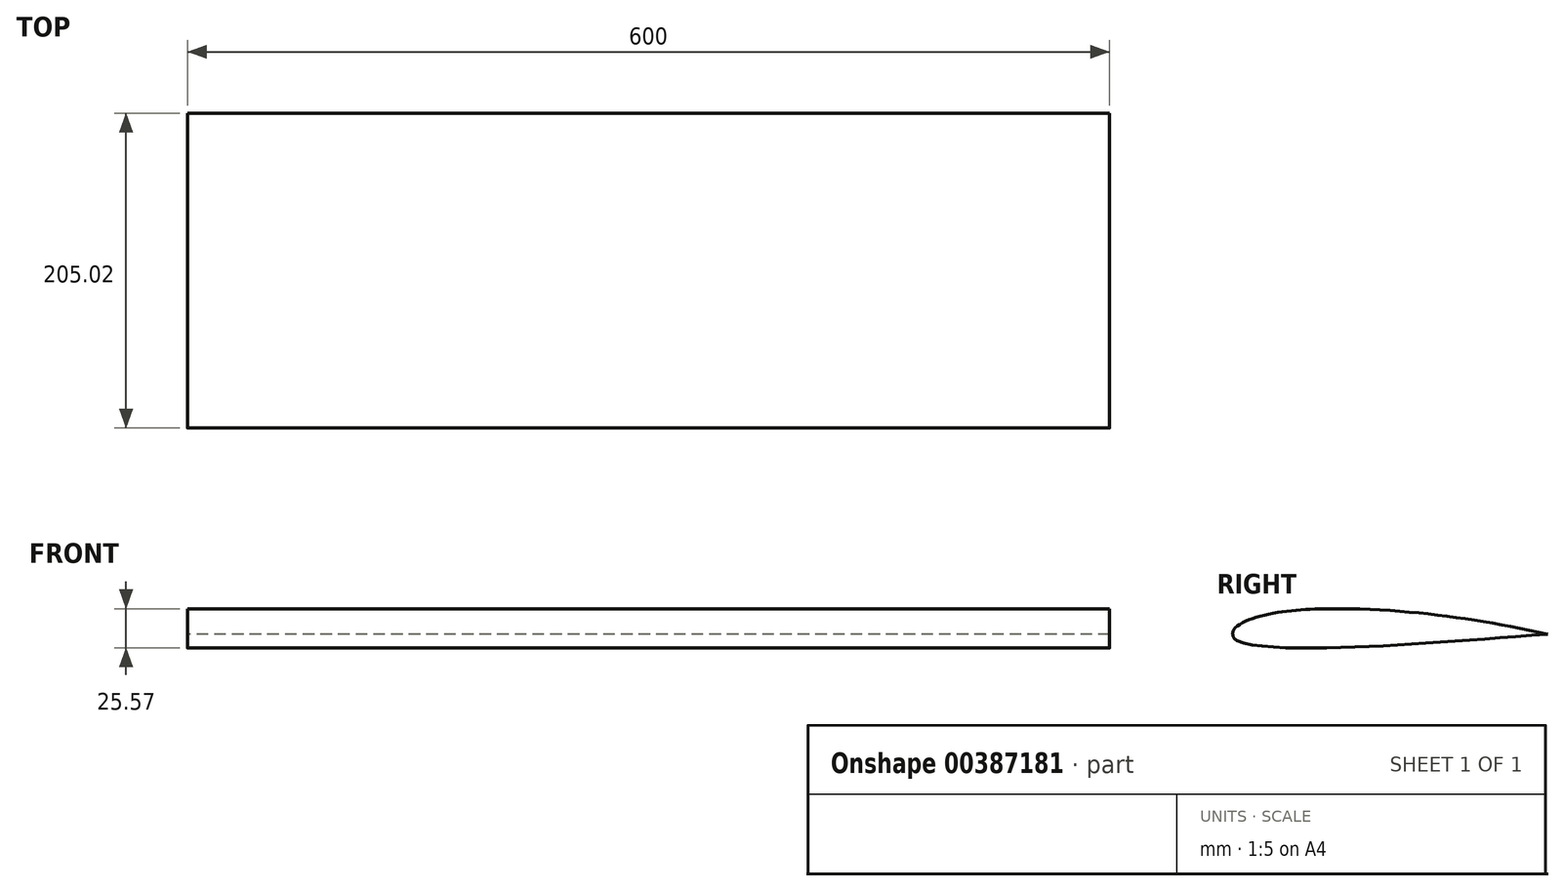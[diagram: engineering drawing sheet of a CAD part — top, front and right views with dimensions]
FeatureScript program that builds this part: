
annotation { "Feature Type Name" : "Feature", "Feature Type Description" : "" }
export const myFeature = defineFeature(function(context is Context, id is Id, definition is map)
    precondition{}
    {
        {
            var Q0;
            Q0=qCreatedBy(makeId("Right.planeOp"),FACE);
            var sketch = newSketch(context, id + "F0", { "sketchPlane" : qUnion([Q0])});
            skSolve(sketch);
        }
        {
            var Q0;
            Q0=qCreatedBy(makeId("Right.planeOp"),FACE);
            var sketch = newSketch(context, id + "F1", { "sketchPlane" : qUnion([Q0])});
            skFitSpline(sketch, "E0", {"points": [v(0, 12.7) * mm, v(-63.5, -3.82) * mm], "startDerivative": vector(-71.79, -0.2) * mm, "endDerivative": vector(-17.43, -38.36) * mm});
            skLineSegment(sketch, "E1", {"start": v(-63.5, -3.82) * mm, "end": v(142.88, -3.82) * mm, "construction": true});
            skFitSpline(sketch, "E2", {"points": [v(0, 12.7) * mm, v(142.88, -3.82) * mm], "startDerivative": vector(161.96, 0.45) * mm, "endDerivative": vector(140.23, -29.51) * mm});
            skFitSpline(sketch, "E3", {"points": [v(-63.5, -3.82) * mm, v(0, -12.7) * mm, v(142.88, -3.82) * mm], "startDerivative": vector(17.1, -66.06) * mm, "endDerivative": vector(264.9, 20.53) * mm});
            skSolve(sketch);
        }
        {
            var Q0;
            Q0=makeQuery(id+"F1.imprint","IMPRINT",FACE,{"disambiguationData":[TD([[makeQuery(id+"F1.imprint","IMPRINT",EDGE,{"derivedFrom":sQuery(id+"F1.wireOp",EDGE,"E0")}),1.0]])]});
            extrude(context, id + "F2", {"entities" : qUnion([Q0]), "depth" : 600 * mm, "symmetric" : true});
        }
        {
            var Q0;
            Q0=makeQuery(id+"F2.opExtrude","SWEPT_EDGE",EDGE,{"disambiguationData":[OSD([sQuery(id+"F1.wireOp",EDGE,"E0"),sQuery(id+"F1.wireOp",EDGE,"E3")])]});
            fillet(context, id + "F3", {"entities" : qUnion([Q0]), "radius" : 5 * mm, "tangentPropagation" : true, "allowEdgeOverflow" : false});
        }
    });
